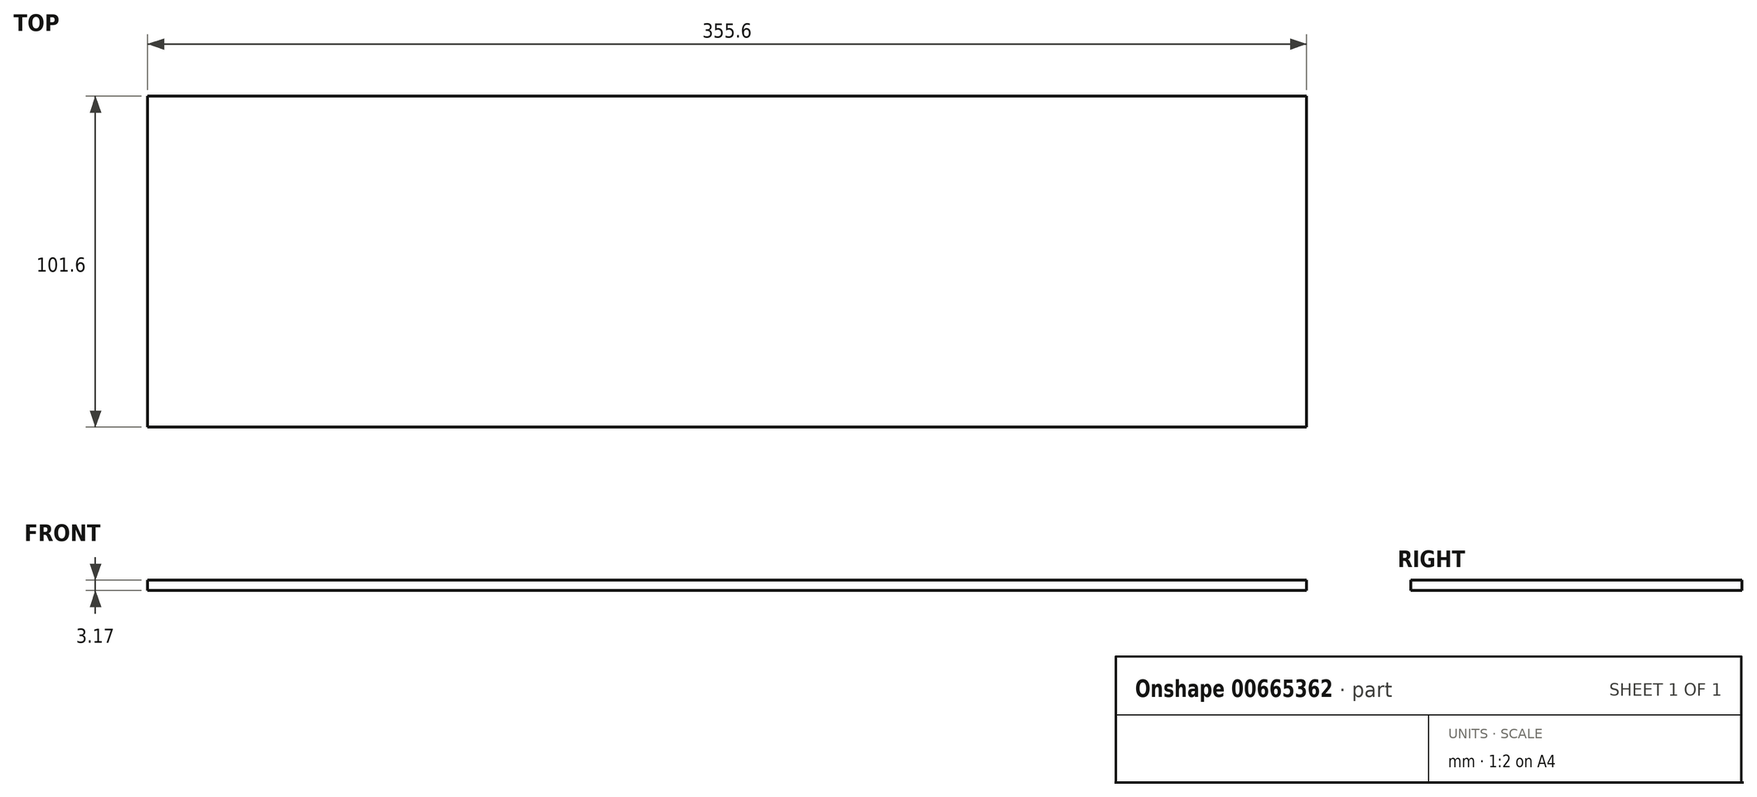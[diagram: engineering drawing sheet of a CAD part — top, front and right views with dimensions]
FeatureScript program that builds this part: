
annotation { "Feature Type Name" : "Feature", "Feature Type Description" : "" }
export const myFeature = defineFeature(function(context is Context, id is Id, definition is map)
    precondition{}
    {
        {
            var Q0;
            Q0=qCreatedBy(makeId("Top.planeOp"),FACE);
            var sketch = newSketch(context, id + "F0", { "sketchPlane" : qUnion([Q0])});
            skLineSegment(sketch, "E0.bottom", {"start": v(-40.75, 72.9) * mm, "end": v(314.85, 72.9) * mm});
            skLineSegment(sketch, "E0.top", {"start": v(-40.75, -28.7) * mm, "end": v(314.85, -28.7) * mm});
            skLineSegment(sketch, "E0.left", {"start": v(-40.75, 72.9) * mm, "end": v(-40.75, -28.7) * mm});
            skLineSegment(sketch, "E0.right", {"start": v(314.85, 72.9) * mm, "end": v(314.85, -28.7) * mm});
            skSolve(sketch);
        }
        {
            var Q0;
            Q0 = qSketchRegion(id + "F0", true);
            extrude(context, id + "F1", {"entities" : qUnion([Q0]), "depth" : 3.17 * mm, "offsetDistance" : 25.4 * mm});
        }
    });
